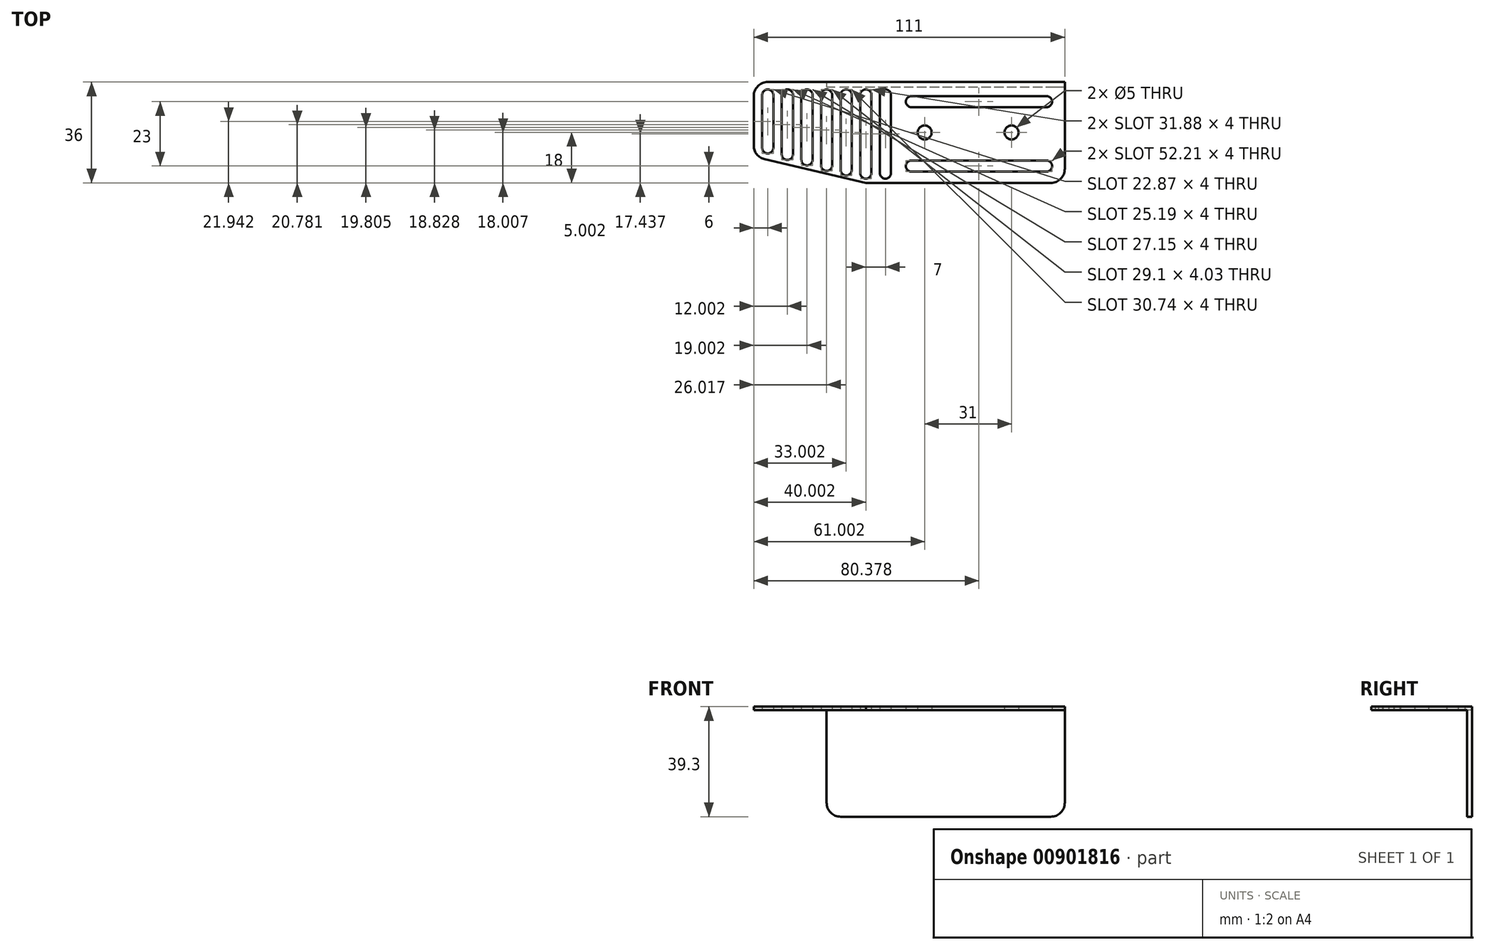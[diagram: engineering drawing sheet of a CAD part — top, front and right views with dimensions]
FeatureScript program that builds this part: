
annotation { "Feature Type Name" : "Feature", "Feature Type Description" : "" }
export const myFeature = defineFeature(function(context is Context, id is Id, definition is map)
    precondition{}
    {
        {
            var Q0;
            Q0=qCreatedBy(makeId("Top.planeOp"),FACE);
            var sketch = newSketch(context, id + "F0", { "sketchPlane" : qUnion([Q0])});
            skLineSegment(sketch, "E0.bottom", {"start": v(-53.8, 18) * mm, "end": v(57.2, 18) * mm});
            skLineSegment(sketch, "E0.right", {"start": v(57.2, 18) * mm, "end": v(57.2, -18) * mm});
            skPoint(sketch, "E1", {"position": v(-27.8, 18) * mm});
            skPoint(sketch, "E2", {"position": v(-13.8, -18) * mm});
            skLineSegment(sketch, "E3", {"start": v(-13.8, -18) * mm, "end": v(57.2, -18) * mm});
            skPoint(sketch, "E4.middle", {"position": v(0, 0) * mm});
            skPoint(sketch, "E5", {"position": v(38.2, 0) * mm});
            skPoint(sketch, "E6", {"position": v(7.2, 0) * mm});
            skCircle(sketch, "E7", {"center": v(7.2, 0) * mm, "radius": 2.5 * mm});
            skCircle(sketch, "E8", {"center": v(38.2, 0) * mm, "radius": 2.5 * mm});
            skLineSegment(sketch, "E9", {"start": v(-50.8, 13.38) * mm, "end": v(-50.8, -5.5) * mm});
            skLineSegment(sketch, "E10", {"start": v(-46.8, 13.38) * mm, "end": v(-46.8, -5.5) * mm});
            skArc(sketch, "E11", {"start": v(-46.8, 13.38) * mm, "mid": v(-48.8, 15.38) * mm, "end": v(-50.8, 13.38) * mm});
            skArc(sketch, "E12", {"start": v(-50.8, -5.5) * mm, "mid": v(-48.8, -7.5) * mm, "end": v(-46.8, -5.5) * mm});
            skLineSegment(sketch, "E13", {"start": v(-43.8, 13.38) * mm, "end": v(-43.8, -7.75) * mm});
            skLineSegment(sketch, "E14", {"start": v(-39.8, 13.38) * mm, "end": v(-39.8, -7.75) * mm});
            skLineSegment(sketch, "E15", {"start": v(-36.8, 13.38) * mm, "end": v(-36.8, -9.77) * mm});
            skLineSegment(sketch, "E16", {"start": v(-32.8, -9.77) * mm, "end": v(-32.8, 13.38) * mm});
            skLineSegment(sketch, "E17", {"start": v(-15.8, 13.38) * mm, "end": v(-15.8, -9.77) * mm});
            skArc(sketch, "E18", {"start": v(-39.8, 13.38) * mm, "mid": v(-41.8, 15.38) * mm, "end": v(-43.8, 13.38) * mm});
            skArc(sketch, "E19", {"start": v(-43.8, -7.75) * mm, "mid": v(-41.8, -9.82) * mm, "end": v(-39.8, -7.75) * mm});
            skArc(sketch, "E20", {"start": v(-32.8, 13.38) * mm, "mid": v(-34.8, 15.38) * mm, "end": v(-36.8, 13.38) * mm});
            skArc(sketch, "E21", {"start": v(-25.8, 13.38) * mm, "mid": v(-27.8, 15.38) * mm, "end": v(-29.8, 13.38) * mm});
            skArc(sketch, "E22", {"start": v(-18.8, 13.38) * mm, "mid": v(-20.8, 15.38) * mm, "end": v(-22.8, 13.38) * mm});
            skArc(sketch, "E23", {"start": v(-11.8, 13.38) * mm, "mid": v(-13.8, 15.38) * mm, "end": v(-15.8, 13.38) * mm});
            skArc(sketch, "E24", {"start": v(-36.8, -9.77) * mm, "mid": v(-34.8, -11.77) * mm, "end": v(-32.8, -9.77) * mm});
            skLineSegment(sketch, "E25", {"start": v(-29.8, 13.38) * mm, "end": v(-29.8, -11.7) * mm});
            skLineSegment(sketch, "E26", {"start": v(-25.77, -11.7) * mm, "end": v(-25.8, 13.38) * mm});
            skLineSegment(sketch, "E27", {"start": v(-22.8, 13.38) * mm, "end": v(-22.8, -13.36) * mm});
            skLineSegment(sketch, "E28", {"start": v(-18.8, -13.36) * mm, "end": v(-18.8, 13.38) * mm});
            skLineSegment(sketch, "E29", {"start": v(-15.8, 13.38) * mm, "end": v(-15.8, -14.5) * mm});
            skLineSegment(sketch, "E30", {"start": v(-11.8, 13.38) * mm, "end": v(-11.8, -14.5) * mm});
            skArc(sketch, "E31", {"start": v(-29.8, -11.7) * mm, "mid": v(-27.78, -13.72) * mm, "end": v(-25.77, -11.7) * mm});
            skArc(sketch, "E32", {"start": v(-22.8, -13.36) * mm, "mid": v(-20.8, -15.36) * mm, "end": v(-18.8, -13.36) * mm});
            skArc(sketch, "E33", {"start": v(-15.8, -14.5) * mm, "mid": v(-13.8, -16.5) * mm, "end": v(-11.8, -14.5) * mm});
            skLineSegment(sketch, "E34", {"start": v(-8.8, 13.38) * mm, "end": v(-8.8, -14.5) * mm});
            skLineSegment(sketch, "E35", {"start": v(-4.8, 13.38) * mm, "end": v(-4.8, -14.5) * mm});
            skArc(sketch, "E36", {"start": v(-4.8, 13.38) * mm, "mid": v(-6.8, 15.38) * mm, "end": v(-8.8, 13.38) * mm});
            skArc(sketch, "E37", {"start": v(-8.8, -14.5) * mm, "mid": v(-6.8, -16.5) * mm, "end": v(-4.8, -14.5) * mm});
            skLineSegment(sketch, "E38", {"start": v(-13.8, -18) * mm, "end": v(-53.8, -8.66) * mm});
            skLineSegment(sketch, "E39", {"start": v(-53.8, 18) * mm, "end": v(-53.8, -8.66) * mm});
            skLineSegment(sketch, "E40", {"start": v(-27.8, 18) * mm, "end": v(-27.8, 16.2) * mm});
            skLineSegment(sketch, "E41", {"start": v(-27.8, 16.2) * mm, "end": v(57.2, 16.2) * mm});
            skLineSegment(sketch, "E42", {"start": v(2.47, 13) * mm, "end": v(50.68, 13) * mm});
            skLineSegment(sketch, "E43", {"start": v(50.68, 9) * mm, "end": v(2.47, 9) * mm});
            skArc(sketch, "E44", {"start": v(2.47, 13) * mm, "mid": v(0.47, 11) * mm, "end": v(2.47, 9) * mm});
            skArc(sketch, "E45", {"start": v(50.68, 9) * mm, "mid": v(52.68, 11) * mm, "end": v(50.68, 13) * mm});
            skPoint(sketch, "E46", {"position": v(50.68, -14) * mm});
            skLineSegment(sketch, "E47", {"start": v(50.68, -14) * mm, "end": v(2.47, -14) * mm});
            skLineSegment(sketch, "E48", {"start": v(2.47, -10) * mm, "end": v(50.68, -10) * mm});
            skArc(sketch, "E49", {"start": v(2.47, -10) * mm, "mid": v(0.47, -12) * mm, "end": v(2.47, -14) * mm});
            skArc(sketch, "E50", {"start": v(50.68, -14) * mm, "mid": v(52.68, -12) * mm, "end": v(50.68, -10) * mm});
            skSolve(sketch);
        }
        {
            var Q0;
            {var subQ1=sQuery(id+"F0.wireOp",EDGE,"E3");Q0=makeQuery(id+"F0.imprint","IMPRINT",FACE,{"disambiguationData":[TD([[makeQuery(id+"F0.imprint","IMPRINT",EDGE,{"derivedFrom":subQ1}),1.0]])]});}
            var Q1;
            {var subQ3=sQuery(id+"F0.wireOp",EDGE,"E40");Q1=makeQuery(id+"F0.imprint","IMPRINT",FACE,{"disambiguationData":[TD([[makeQuery(id+"F0.imprint","IMPRINT",EDGE,{"derivedFrom":subQ3}),1.0]])]});}
            extrude(context, id + "F1", {"entities" : qUnion([Q0, Q1]), "depth" : 1.3 * mm, "offsetDistance" : 25 * mm});
        }
        {
            var Q0;
            {var subQ3=sQuery(id+"F0.wireOp",EDGE,"E40");Q0=makeQuery(id+"F0.imprint","IMPRINT",FACE,{"disambiguationData":[TD([[makeQuery(id+"F0.imprint","IMPRINT",EDGE,{"derivedFrom":subQ3}),1.0]])]});}
            extrude(context, id + "F2", {"entities" : qUnion([Q0]), "operationType" : NewBodyOperationType.ADD, "oppositeDirection" : true, "depth" : 38 * mm, "offsetDistance" : 25 * mm});
        }
        {
            var Q0;
            Q0=makeQuery(id+"F1.opExtrude","SWEPT_EDGE",EDGE,{"disambiguationData":[OSD([sQuery(id+"F0.wireOp",EDGE,"E0.bottom"),sQuery(id+"F0.wireOp",EDGE,"E39")])]});
            var Q1;
            Q1=makeQuery(id+"F1.opExtrude","SWEPT_EDGE",EDGE,{"disambiguationData":[OSD([sQuery(id+"F0.wireOp",EDGE,"E38"),sQuery(id+"F0.wireOp",EDGE,"E39")])]});
            var Q2;
            Q2=makeQuery(id+"F1.opExtrude","SWEPT_EDGE",EDGE,{"disambiguationData":[OSD([sQuery(id+"F0.wireOp",EDGE,"E0.right"),sQuery(id+"F0.wireOp",EDGE,"E3")])]});
            var Q3;
            Q3=makeQuery(id+"F2.opExtrude","CAP_EDGE",EDGE,{"disambiguationData":[OSD([sQuery(id+"F0.wireOp",EDGE,"E0.right")])],"isStart":false});
            var Q4;
            Q4=makeQuery(id+"F2.opExtrude","CAP_EDGE",EDGE,{"disambiguationData":[OSD([sQuery(id+"F0.wireOp",EDGE,"E40")])],"isStart":false});
            fillet(context, id + "F3", {"entities" : qUnion([Q0, Q1, Q2, Q3, Q4]), "radius" : 5 * mm, "tangentPropagation" : true, "allowEdgeOverflow" : false});
        }
    });
